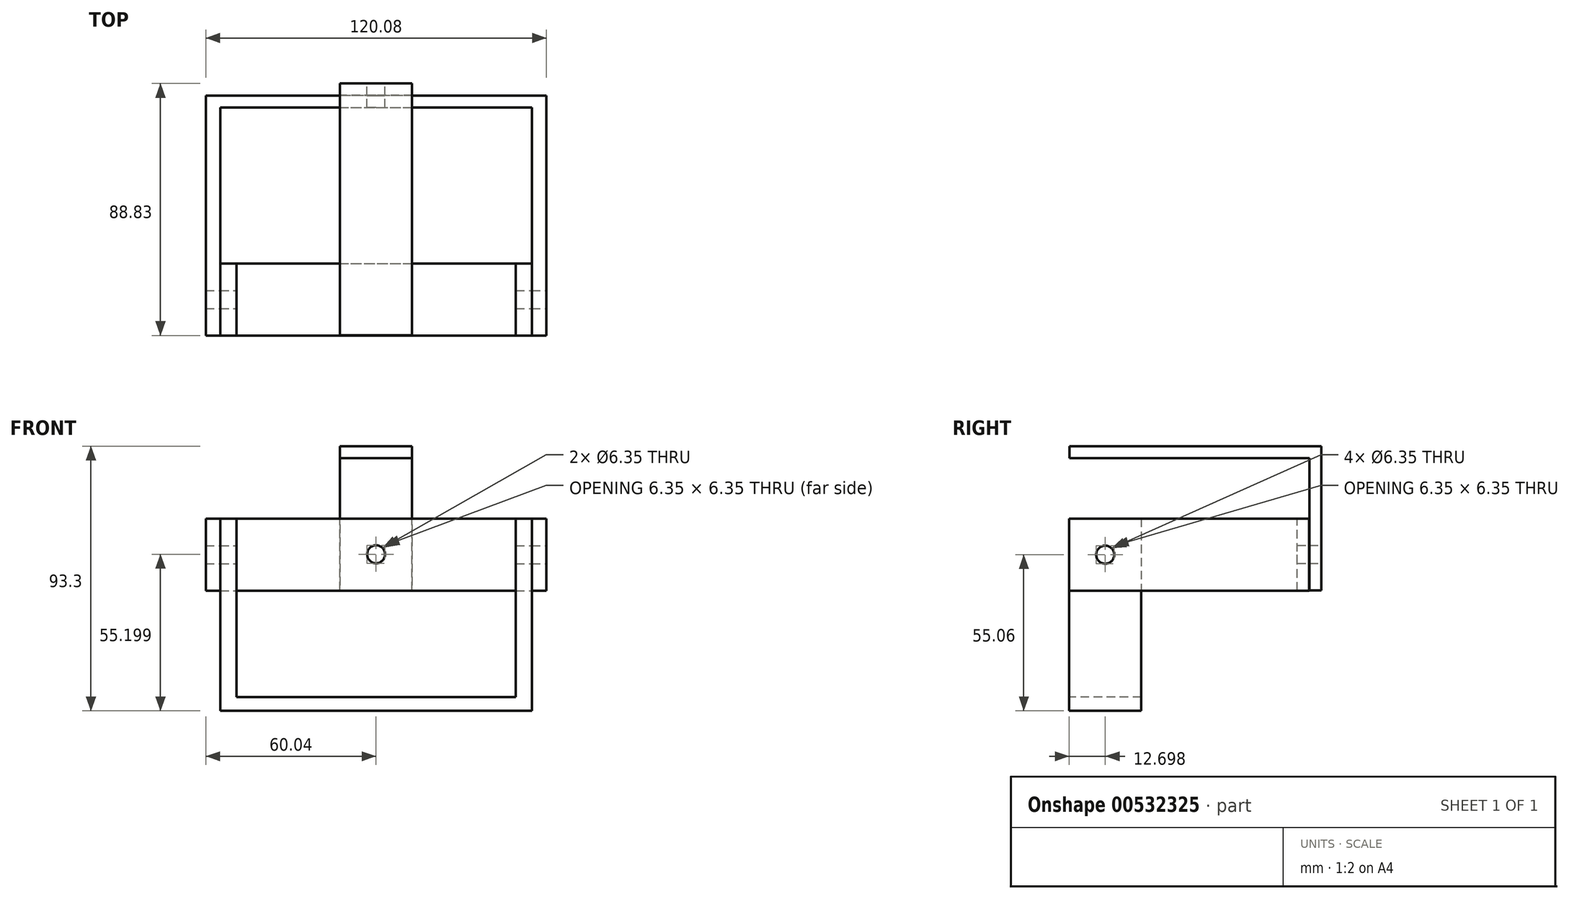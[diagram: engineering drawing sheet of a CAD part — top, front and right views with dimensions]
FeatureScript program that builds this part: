
annotation { "Feature Type Name" : "Feature", "Feature Type Description" : "" }
export const myFeature = defineFeature(function(context is Context, id is Id, definition is map)
    precondition{}
    {
        {
            var Q0;
            Q0=qCreatedBy(makeId("Top.planeOp"),FACE);
            var sketch = newSketch(context, id + "F0", { "sketchPlane" : qUnion([Q0])});
            skLineSegment(sketch, "E0.bottom", {"start": v(60.04, 42.27) * mm, "end": v(-60.04, 42.27) * mm});
            skLineSegment(sketch, "E0.right", {"start": v(-60.04, 42.27) * mm, "end": v(-60.04, -42.27) * mm});
            skPoint(sketch, "E0.middle", {"position": v(0, 0) * mm});
            skLineSegment(sketch, "E1", {"start": v(-54.9, -42.27) * mm, "end": v(-60.04, -42.27) * mm});
            skLineSegment(sketch, "E2", {"start": v(-54.9, -42.27) * mm, "end": v(-54.9, 38.1) * mm});
            skLineSegment(sketch, "E3", {"start": v(-54.9, 38.1) * mm, "end": v(54.9, 38.1) * mm});
            skLineSegment(sketch, "E4.MirrorCS", {"start": v(60.04, 42.27) * mm, "end": v(60.04, -42.27) * mm});
            skLineSegment(sketch, "E5.MirrorCS", {"start": v(54.9, -42.27) * mm, "end": v(54.9, 38.1) * mm});
            skLineSegment(sketch, "E6.MirrorCS", {"start": v(54.9, -42.27) * mm, "end": v(60.04, -42.27) * mm});
            skLineSegment(sketch, "E7", {"start": v(54.9, 38.1) * mm, "end": v(54.9, 38.1) * mm});
            skSolve(sketch);
        }
        {
            var Q0;
            Q0 = qSketchRegion(id + "F0", true);
            extrude(context, id + "F1", {"entities" : qUnion([Q0]), "oppositeDirection" : true, "depth" : 25.4 * mm, "offsetDistance" : 25.4 * mm});
        }
        {
            var Q0;
            Q0=makeQuery(id+"F1.opExtrude","SWEPT_FACE",FACE,{"disambiguationData":[OSD([sQuery(id+"F0.wireOp",EDGE,"E1")])]});
            var sketch = newSketch(context, id + "F2", { "sketchPlane" : qUnion([Q0])});
            skLineSegment(sketch, "E8", {"start": v(-54.9, 0) * mm, "end": v(-54.9, -67.76) * mm});
            skLineSegment(sketch, "E9.MirrorCS", {"start": v(54.9, 0) * mm, "end": v(54.9, -67.76) * mm});
            skLineSegment(sketch, "E10", {"start": v(-54.9, 0) * mm, "end": v(-49.26, 0) * mm});
            skLineSegment(sketch, "E11", {"start": v(-49.26, 0) * mm, "end": v(-49.26, -62.86) * mm});
            skLineSegment(sketch, "E12", {"start": v(-49.26, -62.86) * mm, "end": v(49.26, -62.86) * mm});
            skLineSegment(sketch, "E13", {"start": v(49.26, -62.86) * mm, "end": v(49.26, 0) * mm});
            skLineSegment(sketch, "E14", {"start": v(49.26, 0) * mm, "end": v(54.9, 0) * mm});
            skLineSegment(sketch, "E15", {"start": v(-54.9, -67.76) * mm, "end": v(54.9, -67.76) * mm});
            skSolve(sketch);
        }
        {
            var Q0;
            Q0 = qSketchRegion(id + "F2", true);
            extrude(context, id + "F3", {"entities" : qUnion([Q0]), "oppositeDirection" : true, "depth" : 25.4 * mm, "offsetDistance" : 25.4 * mm});
        }
        {
            var Q0;
            Q0=makeQuery(id+"F1.opExtrude","SWEPT_FACE",FACE,{"disambiguationData":[OSD([sQuery(id+"F0.wireOp",EDGE,"E4.MirrorCS")])]});
            var sketch = newSketch(context, id + "F4", { "sketchPlane" : qUnion([Q0])});
            skPoint(sketch, "E16", {"position": v(-16.87, -25.4) * mm});
            skPoint(sketch, "E17", {"position": v(-29.57, -12.7) * mm});
            skSolve(sketch);
        }
        {
            var Q0;
            Q0=sQuery(id+"F4.wireOp",VERTEX,"E17");
            var Q1;
            Q1=makeQuery(id+"F1.opExtrude","SWEPT_BODY",BODY,{"disambiguationData":[OSD([sQuery(id+"F0.wireOp",EDGE,"E0.bottom"),sQuery(id+"F0.wireOp",EDGE,"E0.right"),sQuery(id+"F0.wireOp",EDGE,"E1"),sQuery(id+"F0.wireOp",EDGE,"E2"),sQuery(id+"F0.wireOp",EDGE,"E3"),sQuery(id+"F0.wireOp",EDGE,"E4.MirrorCS"),sQuery(id+"F0.wireOp",EDGE,"E5.MirrorCS"),sQuery(id+"F0.wireOp",EDGE,"E6.MirrorCS")])]});
            var Q2;
            Q2=makeQuery(id+"F3.opExtrude","SWEPT_BODY",BODY,{"disambiguationData":[OSD([sQuery(id+"F2.wireOp",EDGE,"E8"),sQuery(id+"F2.wireOp",EDGE,"E9.MirrorCS"),sQuery(id+"F2.wireOp",EDGE,"E10"),sQuery(id+"F2.wireOp",EDGE,"E11"),sQuery(id+"F2.wireOp",EDGE,"E12"),sQuery(id+"F2.wireOp",EDGE,"E13"),sQuery(id+"F2.wireOp",EDGE,"E14"),sQuery(id+"F2.wireOp",EDGE,"E15")])]});
            hole(context, id + "F5", {"style" : HoleStyle.SIMPLE, "endStyle" : HoleEndStyle.THROUGH, "holeDiameter" : 6.35 * mm, "isTappedThrough" : true, "tappedDepth" : 12.7 * mm, "tapClearance" : 3, "locations" : qUnion([Q0]), "scope" : qUnion([Q1, Q2])});
        }
        {
            var Q0;
            Q0=qCreatedBy(makeId("Right.planeOp"),FACE);
            var sketch = newSketch(context, id + "F6", { "sketchPlane" : qUnion([Q0])});
            skLineSegment(sketch, "E18", {"start": v(42.4, 9.43) * mm, "end": v(-42.15, 9.43) * mm});
            skLineSegment(sketch, "E19", {"start": v(-42.15, 9.43) * mm, "end": v(-42.15, 13.6) * mm});
            skLineSegment(sketch, "E20", {"start": v(-42.15, 13.6) * mm, "end": v(46.56, 13.6) * mm});
            skLineSegment(sketch, "E21", {"start": v(46.56, 13.6) * mm, "end": v(46.56, -37.2) * mm});
            skLineSegment(sketch, "E22", {"start": v(46.56, -37.2) * mm, "end": v(42.4, -37.2) * mm});
            skLineSegment(sketch, "E23", {"start": v(42.4, -37.2) * mm, "end": v(42.4, 9.43) * mm});
            skSolve(sketch);
        }
        {
            var Q0;
            Q0 = qSketchRegion(id + "F6", true);
            extrude(context, id + "F7", {"entities" : qUnion([Q0]), "endBound" : BoundingType.SYMMETRIC, "depth" : 25.4 * mm, "offsetDistance" : 25.4 * mm});
        }
        {
            var Q0;
            Q0=makeQuery(id+"F7.opExtrude","SWEPT_BODY",BODY,{"disambiguationData":[OSD([sQuery(id+"F6.wireOp",EDGE,"E18"),sQuery(id+"F6.wireOp",EDGE,"E19"),sQuery(id+"F6.wireOp",EDGE,"E20"),sQuery(id+"F6.wireOp",EDGE,"E21"),sQuery(id+"F6.wireOp",EDGE,"E22"),sQuery(id+"F6.wireOp",EDGE,"E23")])]});
            var Q1;
            Q1=makeQuery(id+"F7.opExtrude","CAP_VERTEX",VERTEX,{"disambiguationData":[OSD([sQuery(id+"F6.wireOp",EDGE,"E21"),sQuery(id+"F6.wireOp",EDGE,"E22")])],"isStart":false});
            var Q2;
            Q2=makeQuery(id+"F7.opExtrude","CAP_EDGE",EDGE,{"disambiguationData":[OSD([sQuery(id+"F6.wireOp",EDGE,"E21")])],"isStart":false});
            transform(context, id + "F8", {"entities" : qUnion([Q0]), "transformType" : TransformType.TRANSLATION_DISTANCE, "transformDirection" : qUnion([Q1, Q2]), "distance" : 11.94 * mm, "oppositeDirection" : true, "makeCopy" : false});
        }
        {
            var Q0;
            Q0=makeQuery(id+"F7.opExtrude","SWEPT_FACE",FACE,{"disambiguationData":[OSD([sQuery(id+"F6.wireOp",EDGE,"E21")])]});
            var sketch = newSketch(context, id + "F9", { "sketchPlane" : qUnion([Q0])});
            skPoint(sketch, "E24", {"position": v(0, -12.56) * mm});
            skPoint(sketch, "E24.positionSnap0", {"position": v(0, -25.26) * mm});
            skSolve(sketch);
        }
        {
            var Q0;
            Q0=sQuery(id+"F9.wireOp",VERTEX,"E24");
            var Q1;
            Q1=makeQuery(id+"F1.opExtrude","SWEPT_BODY",BODY,{"disambiguationData":[OSD([sQuery(id+"F0.wireOp",EDGE,"E0.bottom"),sQuery(id+"F0.wireOp",EDGE,"E0.right"),sQuery(id+"F0.wireOp",EDGE,"E1"),sQuery(id+"F0.wireOp",EDGE,"E2"),sQuery(id+"F0.wireOp",EDGE,"E3"),sQuery(id+"F0.wireOp",EDGE,"E4.MirrorCS"),sQuery(id+"F0.wireOp",EDGE,"E5.MirrorCS"),sQuery(id+"F0.wireOp",EDGE,"E6.MirrorCS")])]});
            var Q2;
            Q2=makeQuery(id+"F7.opExtrude","SWEPT_BODY",BODY,{"disambiguationData":[OSD([sQuery(id+"F6.wireOp",EDGE,"E18"),sQuery(id+"F6.wireOp",EDGE,"E19"),sQuery(id+"F6.wireOp",EDGE,"E20"),sQuery(id+"F6.wireOp",EDGE,"E21"),sQuery(id+"F6.wireOp",EDGE,"E22"),sQuery(id+"F6.wireOp",EDGE,"E23")])]});
            hole(context, id + "F10", {"style" : HoleStyle.SIMPLE, "endStyle" : HoleEndStyle.THROUGH, "holeDiameter" : 6.35 * mm, "isTappedThrough" : true, "tappedDepth" : 12.7 * mm, "tapClearance" : 3, "locations" : qUnion([Q0]), "scope" : qUnion([Q1, Q2])});
        }
    });
